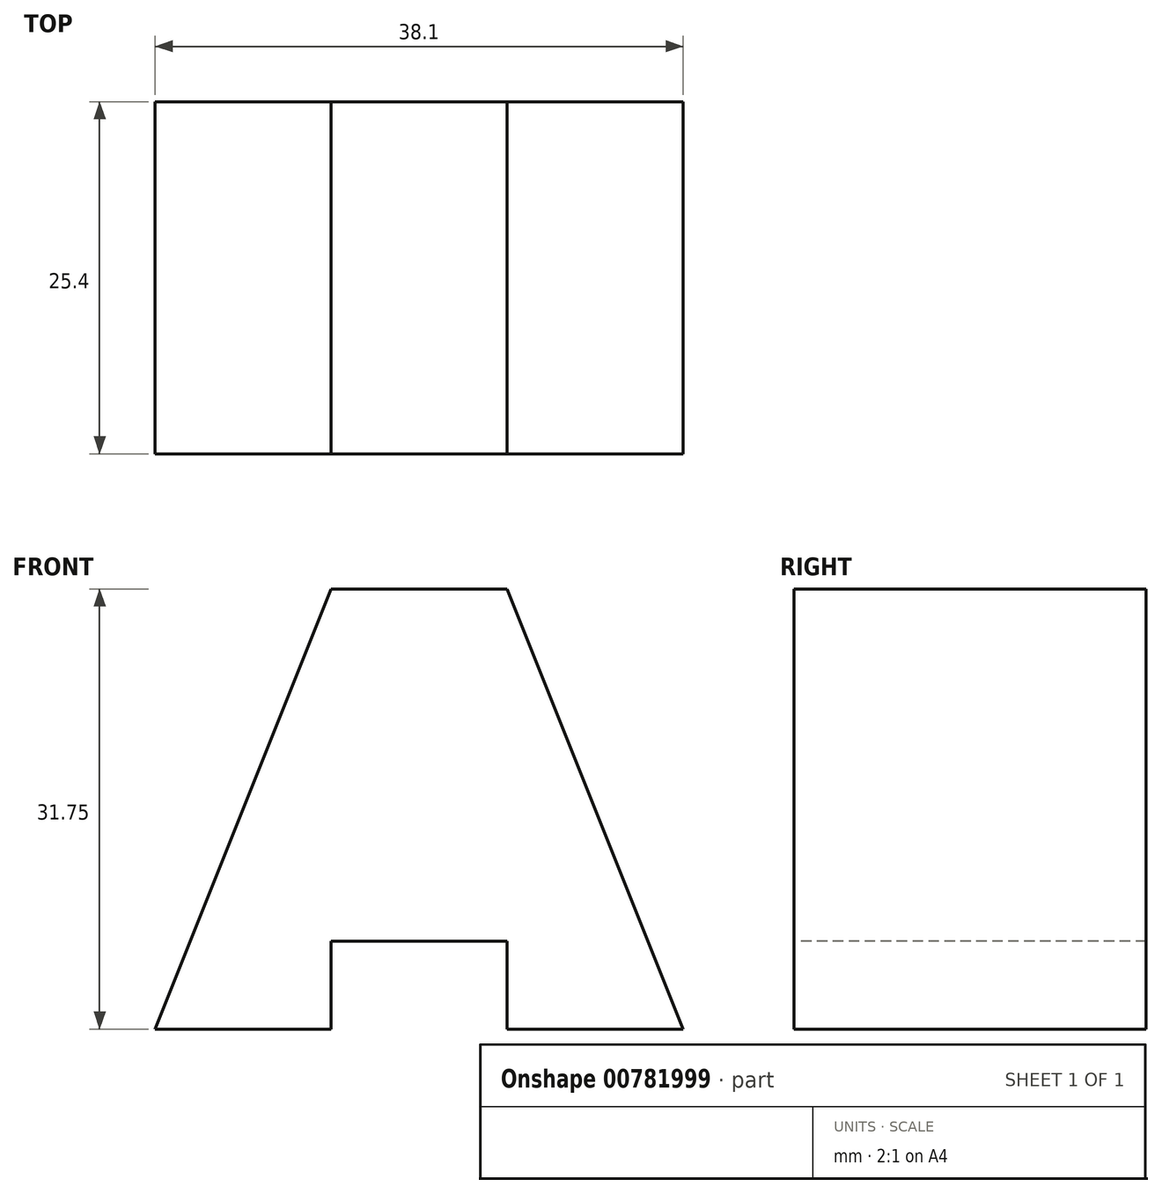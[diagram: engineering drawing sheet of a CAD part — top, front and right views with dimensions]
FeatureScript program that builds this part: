
annotation { "Feature Type Name" : "Feature", "Feature Type Description" : "" }
export const myFeature = defineFeature(function(context is Context, id is Id, definition is map)
    precondition{}
    {
        {
            var Q0;
            Q0=qCreatedBy(makeId("Front.planeOp"),FACE);
            var sketch = newSketch(context, id + "F0", { "sketchPlane" : qUnion([Q0])});
            skLineSegment(sketch, "E0", {"start": v(0, 31.75) * mm, "end": v(0, 0) * mm});
            skLineSegment(sketch, "E1", {"start": v(0, 0) * mm, "end": v(38.1, 0) * mm});
            skLineSegment(sketch, "E2", {"start": v(38.1, 0) * mm, "end": v(38.1, 31.75) * mm});
            skLineSegment(sketch, "E3", {"start": v(0, 31.75) * mm, "end": v(38.1, 31.75) * mm});
            skSolve(sketch);
        }
        {
            var Q0;
            Q0=makeQuery(id+"F0.imprint","IMPRINT",FACE,{"disambiguationData":[TD([[makeQuery(id+"F0.imprint","IMPRINT",EDGE,{"derivedFrom":sQuery(id+"F0.wireOp",EDGE,"E0")}),1.0]])]});
            var Q1;
            Q1=qSketchRegion(id+"F2",true);
            extrude(context, id + "F1", {"entities" : qUnion([Q0, Q1]), "depth" : 25.4 * mm, "offsetDistance" : 25.4 * mm});
        }
        {
            var Q0;
            Q0=qCreatedBy(makeId("Front.planeOp"),FACE);
            var sketch = newSketch(context, id + "F2", { "sketchPlane" : qUnion([Q0])});
            skLineSegment(sketch, "E4", {"start": v(38.15, 0) * mm, "end": v(26.35, 31.74) * mm});
            skLineSegment(sketch, "E5", {"start": v(12.7, 31.74) * mm, "end": v(0, 0) * mm});
            skSolve(sketch);
        }
        {
            var Q0;
            Q0=qSketchRegion(id+"F0",true);
            extrude(context, id + "F3", {"entities" : qUnion([Q0]), "operationType" : NewBodyOperationType.ADD, "depth" : 25.4 * mm, "offsetDistance" : 25.4 * mm});
        }
        {
            var Q0;
            Q0=qSketchRegion(id+"F0",true);
            extrude(context, id + "F4", {"entities" : qUnion([Q0]), "operationType" : NewBodyOperationType.ADD, "depth" : 25.4 * mm, "offsetDistance" : 25.4 * mm});
        }
        {
            var Q0;
            Q0=makeQuery(id+"F1.opExtrude","CAP_FACE",FACE,{"disambiguationData":[OSD([sQuery(id+"F0.wireOp",EDGE,"E0"),sQuery(id+"F0.wireOp",EDGE,"E1"),sQuery(id+"F0.wireOp",EDGE,"E2"),sQuery(id+"F0.wireOp",EDGE,"E3")])],"isStart":false});
            var sketch = newSketch(context, id + "F5", { "sketchPlane" : qUnion([Q0])});
            skLineSegment(sketch, "E6", {"start": v(0, 0) * mm, "end": v(12.7, 31.75) * mm});
            skLineSegment(sketch, "E7", {"start": v(38.1, 0) * mm, "end": v(25.4, 31.75) * mm});
            skLineSegment(sketch, "E8", {"start": v(12.7, 0) * mm, "end": v(12.7, 6.35) * mm});
            skLineSegment(sketch, "E9", {"start": v(12.7, 6.35) * mm, "end": v(25.4, 6.35) * mm});
            skLineSegment(sketch, "E10", {"start": v(25.4, 6.35) * mm, "end": v(25.4, 0) * mm});
            skSolve(sketch);
        }
        {
            var Q0;
            Q0=qSketchRegion(id+"F5",true);
            var Q1;
            {var subQ0=sQuery(id+"F5.wireOp",EDGE,"E6");Q1=makeQuery(id+"F5.imprint","IMPRINT",FACE,{"disambiguationData":[TD([[makeQuery(id+"F5.imprint","IMPRINT",EDGE,{"derivedFrom":subQ0}),1.0]])]});}
            var Q2;
            {var subQ0=sQuery(id+"F5.wireOp",EDGE,"E7");Q2=makeQuery(id+"F5.imprint","IMPRINT",FACE,{"disambiguationData":[TD([[makeQuery(id+"F5.imprint","IMPRINT",EDGE,{"derivedFrom":subQ0}),-1.0]])]});}
            var Q3;
            {var subQ0=sQuery(id+"F5.wireOp",EDGE,"E8");Q3=makeQuery(id+"F5.imprint","IMPRINT",FACE,{"disambiguationData":[TD([[makeQuery(id+"F5.imprint","IMPRINT",EDGE,{"derivedFrom":subQ0}),-1.0]])]});}
            extrude(context, id + "F6", {"entities" : qUnion([Q0, Q1, Q2, Q3]), "operationType" : NewBodyOperationType.REMOVE, "endBound" : BoundingType.THROUGH_ALL, "oppositeDirection" : true, "depth" : 25.4 * mm, "offsetDistance" : 25.4 * mm});
        }
    });
